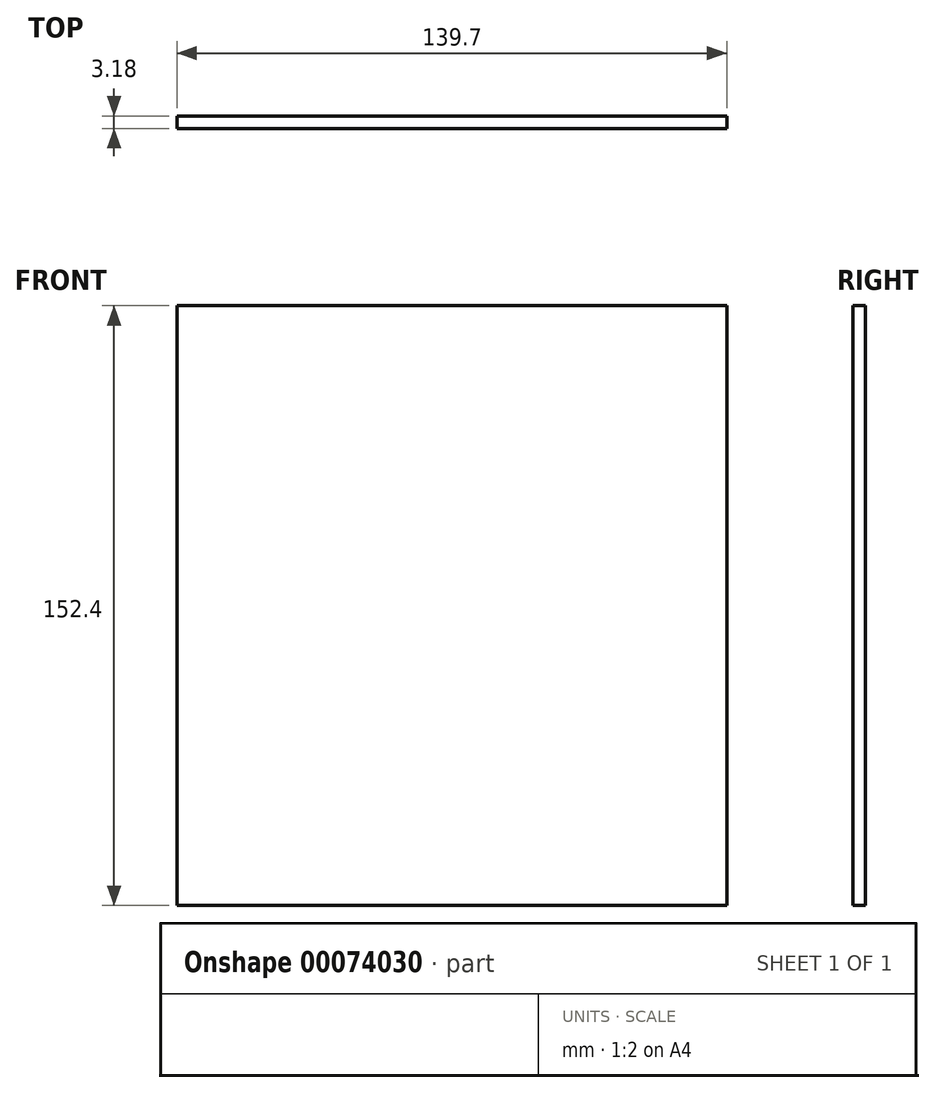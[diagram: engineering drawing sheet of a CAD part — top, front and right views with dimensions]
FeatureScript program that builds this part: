
annotation { "Feature Type Name" : "Feature", "Feature Type Description" : "" }
export const myFeature = defineFeature(function(context is Context, id is Id, definition is map)
    precondition{}
    {
        {
            var Q0;
            Q0=qCreatedBy(makeId("Front.planeOp"),FACE);
            var sketch = newSketch(context, id + "F0", { "sketchPlane" : qUnion([Q0])});
            skLineSegment(sketch, "E0.bottom", {"start": v(-87.49, 68.9) * mm, "end": v(52.21, 68.9) * mm});
            skLineSegment(sketch, "E0.top", {"start": v(-87.49, -83.5) * mm, "end": v(52.21, -83.5) * mm});
            skLineSegment(sketch, "E0.left", {"start": v(-87.49, 68.9) * mm, "end": v(-87.49, -83.5) * mm});
            skLineSegment(sketch, "E0.right", {"start": v(52.21, 68.9) * mm, "end": v(52.21, -83.5) * mm});
            skSolve(sketch);
        }
        {
            var Q0;
            Q0 = qSketchRegion(id + "F0", true);
            extrude(context, id + "F1", {"entities" : qUnion([Q0]), "depth" : 3.17 * mm, "symmetric" : true});
        }
    });
